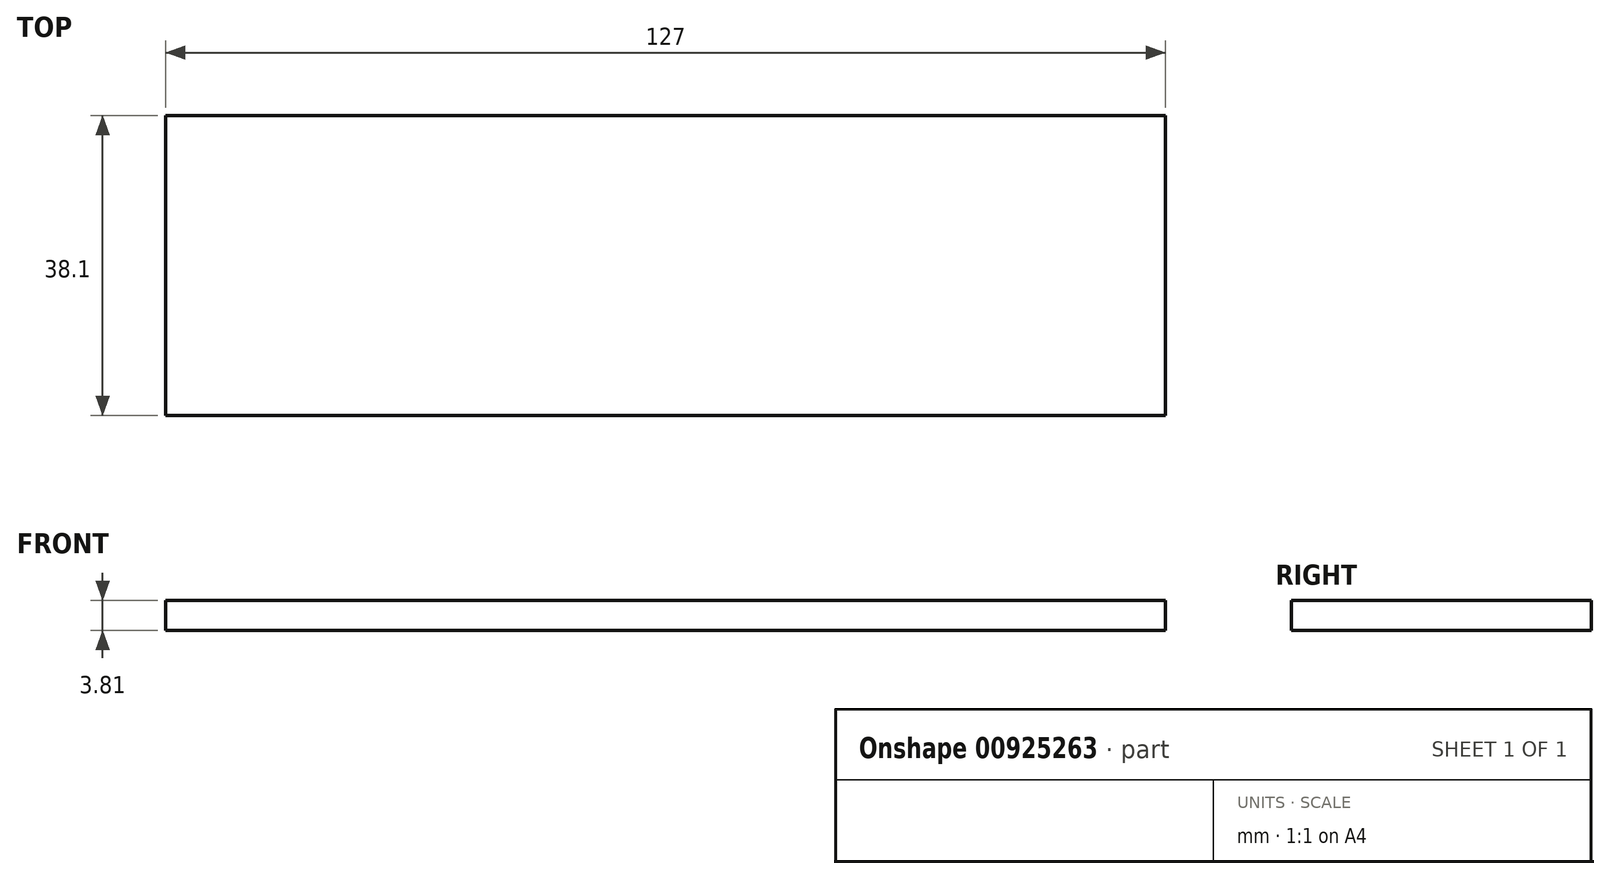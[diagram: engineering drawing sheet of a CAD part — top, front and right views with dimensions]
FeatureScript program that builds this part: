
annotation { "Feature Type Name" : "Feature", "Feature Type Description" : "" }
export const myFeature = defineFeature(function(context is Context, id is Id, definition is map)
    precondition{}
    {
        {
            var Q0;
            Q0=qCreatedBy(makeId("Top.planeOp"),FACE);
            var sketch = newSketch(context, id + "F0", { "sketchPlane" : qUnion([Q0])});
            skLineSegment(sketch, "E0.bottom", {"start": v(-34.34, 22.88) * mm, "end": v(92.66, 22.88) * mm});
            skLineSegment(sketch, "E0.top", {"start": v(-34.34, -15.22) * mm, "end": v(92.66, -15.22) * mm});
            skLineSegment(sketch, "E0.left", {"start": v(-34.34, 22.88) * mm, "end": v(-34.34, -15.22) * mm});
            skLineSegment(sketch, "E0.right", {"start": v(92.66, 22.88) * mm, "end": v(92.66, -15.22) * mm});
            skSolve(sketch);
        }
        {
            var Q0;
            Q0=makeQuery(id+"F0.imprint","IMPRINT",FACE,{"disambiguationData":[TD([[makeQuery(id+"F0.imprint","IMPRINT",EDGE,{"derivedFrom":sQuery(id+"F0.wireOp",EDGE,"E0.bottom")}),-1.0]])]});
            extrude(context, id + "F1", {"entities" : qUnion([Q0]), "depth" : 3.8 * mm, "offsetDistance" : 25.4 * mm});
        }
    });
